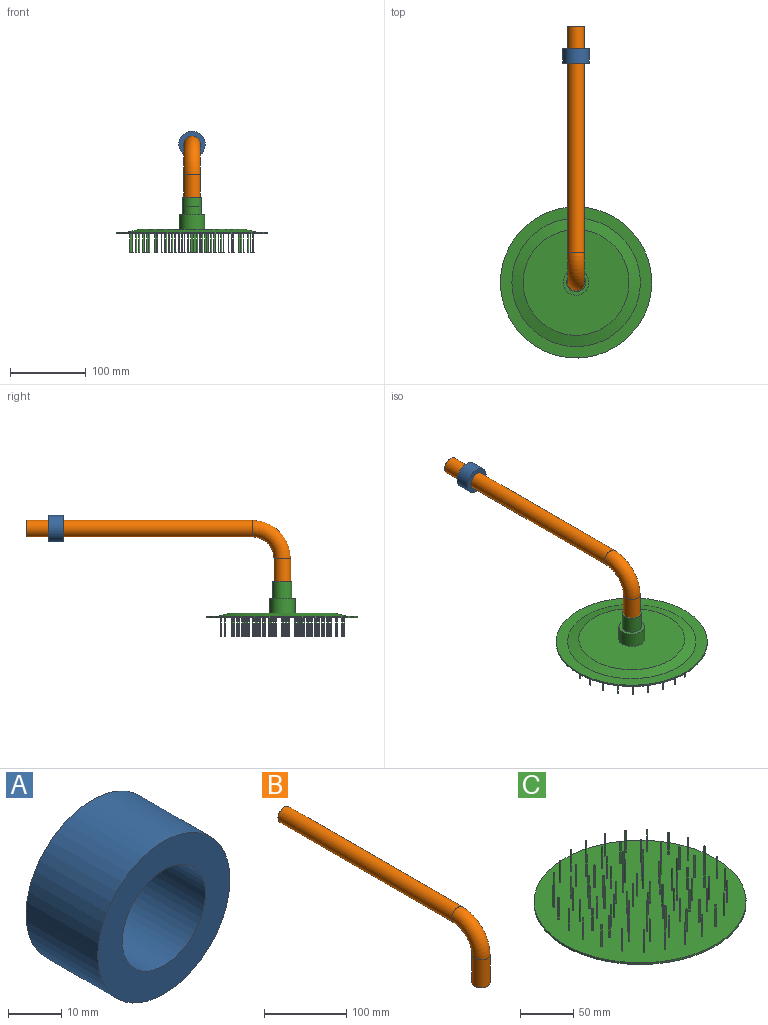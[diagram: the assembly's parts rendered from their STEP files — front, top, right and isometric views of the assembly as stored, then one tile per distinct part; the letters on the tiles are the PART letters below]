
ASSEMBLY  parts=3 mates=2
PART A: 4 faces, bbox 35x19x35 mm
  f0: cylinder r=11mm len=22mm, axis (0,1,0), area 1313.2mm2, adj f2,f3
  f1: cylinder r=17.5mm len=35mm, axis (0,1,0), area 2089.2mm2, adj f2,f3
  f2: plane 35x35mm, normal (0,-1,0), area 582mm2, adj f0,f1
  f3: plane 35x35mm, normal (0,1,0), area 582mm2, adj f0,f1
PART B: 5 faces, bbox 22x354.2x96.7 mm
  f0: plane 22x22mm, normal (0,1,0), area 380.1mm2, adj f2
  f1: plane 22x22mm, normal (0,0,-1), area 380.1mm2, adj f4
  f2: cylinder r=11mm len=299mm, axis (0,-1,0), area 20665.4mm2, adj f0,f3
  f3: torus R=40mm, axis (1,0,0), area 4342.6mm2, adj f2,f4
  f4: cylinder r=11mm len=41.5mm, axis (0,0,-1), area 2868.3mm2, adj f1,f3
PART C: 181 faces, bbox 200x200x73.5 mm
  f0: cylinder r=100mm len=200mm, axis (0,0,-1), area 1256.6mm2, adj f1,f2
  f1: plane 200x200mm, normal (0,0,1), area 31318.7mm2, adj f0,f9,f11,f13,f15,f17,f19,f21
  f2: plane 200x200mm, normal (0,0,-1), area 8756.2mm2, adj f0,f3
  f3: cone r=70mm half-angle=75deg, axis (0,0,1), area 7522.2mm2, adj f2,f4
  f4: plane 140x140mm, normal (0,0,-1), area 14485.9mm2, adj f3,f5
  f5: cylinder r=17mm len=34mm, axis (0,0,1), area 2136.3mm2, adj f4,f6
  f6: plane 34x34mm, normal (0,0,-1), area 417mm2, adj f5,f7
  f7: cylinder r=12.5mm len=25mm, axis (0,0,1), area 1767.1mm2, adj f6,f8
  f8: plane 25x25mm, normal (0,0,-1), area 490.9mm2, adj f7
  f9: cylinder r=0.6mm len=25mm, axis (0,0,-1), area 94.2mm2, adj f1,f10
  f10: plane 1.2x1.2mm, normal (0,0,1), area 1.1mm2, adj f9
  f11: cylinder r=0.6mm len=25mm, axis (0,0,-1), area 94.2mm2, adj f1,f12
  f12: plane 1.2x1.2mm, normal (0,0,1), area 1.1mm2, adj f11
  f13: cylinder r=0.6mm len=25mm, axis (0,0,-1), area 94.2mm2, adj f1,f14
  f14: plane 1.2x1.2mm, normal (0,0,1), area 1.1mm2, adj f13
  f15: cylinder r=0.6mm len=25mm, axis (0,0,-1), area 94.2mm2, adj f1,f16
  f16: plane 1.2x1.2mm, normal (0,0,1), area 1.1mm2, adj f15
  f17: cylinder r=0.6mm len=25mm, axis (0,0,-1), area 94.2mm2, adj f1,f18
  f18: plane 1.2x1.2mm, normal (0,0,1), area 1.1mm2, adj f17
  f19: cylinder r=0.6mm len=25mm, axis (0,0,-1), area 94.2mm2, adj f1,f20
  f20: plane 1.2x1.2mm, normal (0,0,1), area 1.1mm2, adj f19
  f21: cylinder r=0.6mm len=25mm, axis (0,0,-1), area 94.2mm2, adj f1,f22
  f22: plane 1.2x1.2mm, normal (0,0,1), area 1.1mm2, adj f21
  f23: cylinder r=0.6mm len=25mm, axis (0,0,-1), area 94.2mm2, adj f1,f24
  f24: plane 1.2x1.2mm, normal (0,0,1), area 1.1mm2, adj f23
  f25: cylinder r=0.6mm len=25mm, axis (0,0,-1), area 94.2mm2, adj f1,f26
  f26: plane 1.2x1.2mm, normal (0,0,1), area 1.1mm2, adj f25
  f27: cylinder r=0.6mm len=25mm, axis (0,0,-1), area 94.2mm2, adj f1,f28
  f28: plane 1.2x1.2mm, normal (0,0,1), area 1.1mm2, adj f27
  f29: cylinder r=0.6mm len=25mm, axis (0,0,-1), area 94.2mm2, adj f1,f30
  f30: plane 1.2x1.2mm, normal (0,0,1), area 1.1mm2, adj f29
  f31: cylinder r=0.6mm len=25mm, axis (0,0,-1), area 94.2mm2, adj f1,f32
  f32: plane 1.2x1.2mm, normal (0,0,1), area 1.1mm2, adj f31
  f33: cylinder r=0.6mm len=25mm, axis (0,0,-1), area 94.2mm2, adj f1,f34
  f34: plane 1.2x1.2mm, normal (0,0,1), area 1.1mm2, adj f33
  f35: cylinder r=0.6mm len=25mm, axis (0,0,-1), area 94.2mm2, adj f1,f36
  f36: plane 1.2x1.2mm, normal (0,0,1), area 1.1mm2, adj f35
  f37: cylinder r=0.6mm len=25mm, axis (0,0,-1), area 94.2mm2, adj f1,f38
  f38: plane 1.2x1.2mm, normal (0,0,1), area 1.1mm2, adj f37
  f39: cylinder r=0.6mm len=25mm, axis (0,0,-1), area 94.2mm2, adj f1,f40
  f40: plane 1.2x1.2mm, normal (0,0,1), area 1.1mm2, adj f39
  f41: cylinder r=0.6mm len=25mm, axis (0,0,-1), area 94.2mm2, adj f1,f42
  f42: plane 1.2x1.2mm, normal (0,0,1), area 1.1mm2, adj f41
  f43: cylinder r=0.6mm len=25mm, axis (0,0,-1), area 94.2mm2, adj f1,f44
  f44: plane 1.2x1.2mm, normal (0,0,1), area 1.1mm2, adj f43
  f45: cylinder r=0.6mm len=25mm, axis (0,0,-1), area 94.2mm2, adj f1,f46
  f46: plane 1.2x1.2mm, normal (0,0,1), area 1.1mm2, adj f45
  f47: cylinder r=0.6mm len=25mm, axis (0,0,-1), area 94.2mm2, adj f1,f48
  f48: plane 1.2x1.2mm, normal (0,0,1), area 1.1mm2, adj f47
  f49: cylinder r=0.6mm len=25mm, axis (0,0,-1), area 94.2mm2, adj f1,f50
  f50: plane 1.2x1.2mm, normal (0,0,1), area 1.1mm2, adj f49
  f51: cylinder r=0.6mm len=25mm, axis (0,0,-1), area 94.2mm2, adj f1,f52
  f52: plane 1.2x1.2mm, normal (0,0,1), area 1.1mm2, adj f51
  f53: cylinder r=0.6mm len=25mm, axis (0,0,-1), area 94.2mm2, adj f1,f54
  f54: plane 1.2x1.2mm, normal (0,0,1), area 1.1mm2, adj f53
  f55: cylinder r=0.6mm len=25mm, axis (0,0,-1), area 94.2mm2, adj f1,f56
  f56: plane 1.2x1.2mm, normal (0,0,1), area 1.1mm2, adj f55
  f57: cylinder r=0.6mm len=25mm, axis (0,0,-1), area 94.2mm2, adj f1,f58
  f58: plane 1.2x1.2mm, normal (0,0,1), area 1.1mm2, adj f57
  f59: cylinder r=0.6mm len=25mm, axis (0,0,-1), area 94.2mm2, adj f1,f60
  f60: plane 1.2x1.2mm, normal (0,0,1), area 1.1mm2, adj f59
  f61: cylinder r=0.6mm len=25mm, axis (0,0,-1), area 94.2mm2, adj f1,f62
  f62: plane 1.2x1.2mm, normal (0,0,1), area 1.1mm2, adj f61
  f63: cylinder r=0.6mm len=25mm, axis (0,0,-1), area 94.2mm2, adj f1,f64
  f64: plane 1.2x1.2mm, normal (0,0,1), area 1.1mm2, adj f63
  f65: cylinder r=0.6mm len=25mm, axis (0,0,-1), area 94.2mm2, adj f1,f66
  f66: plane 1.2x1.2mm, normal (0,0,1), area 1.1mm2, adj f65
  f67: cylinder r=0.6mm len=25mm, axis (0,0,-1), area 94.2mm2, adj f1,f68
  f68: plane 1.2x1.2mm, normal (0,0,1), area 1.1mm2, adj f67
  f69: cylinder r=0.6mm len=25mm, axis (0,0,-1), area 94.2mm2, adj f1,f70
  f70: plane 1.2x1.2mm, normal (0,0,1), area 1.1mm2, adj f69
  f71: cylinder r=0.6mm len=25mm, axis (0,0,-1), area 94.2mm2, adj f1,f72
  f72: plane 1.2x1.2mm, normal (0,0,1), area 1.1mm2, adj f71
  f73: cylinder r=0.6mm len=25mm, axis (0,0,-1), area 94.2mm2, adj f1,f74
  f74: plane 1.2x1.2mm, normal (0,0,1), area 1.1mm2, adj f73
  f75: cylinder r=0.6mm len=25mm, axis (0,0,-1), area 94.2mm2, adj f1,f76
  f76: plane 1.2x1.2mm, normal (0,0,1), area 1.1mm2, adj f75
  f77: cylinder r=0.6mm len=25mm, axis (0,0,-1), area 94.2mm2, adj f1,f78
  f78: plane 1.2x1.2mm, normal (0,0,1), area 1.1mm2, adj f77
  f79: cylinder r=0.6mm len=25mm, axis (0,0,-1), area 94.2mm2, adj f1,f80
  f80: plane 1.2x1.2mm, normal (0,0,1), area 1.1mm2, adj f79
  f81: cylinder r=0.6mm len=25mm, axis (0,0,-1), area 94.2mm2, adj f1,f82
  f82: plane 1.2x1.2mm, normal (0,0,1), area 1.1mm2, adj f81
  f83: cylinder r=0.6mm len=25mm, axis (0,0,-1), area 94.2mm2, adj f1,f84
  f84: plane 1.2x1.2mm, normal (0,0,1), area 1.1mm2, adj f83
  f85: cylinder r=0.6mm len=25mm, axis (0,0,-1), area 94.2mm2, adj f1,f86
  f86: plane 1.2x1.2mm, normal (0,0,1), area 1.1mm2, adj f85
  f87: cylinder r=0.6mm len=25mm, axis (0,0,-1), area 94.2mm2, adj f1,f88
  f88: plane 1.2x1.2mm, normal (0,0,1), area 1.1mm2, adj f87
  f89: cylinder r=0.6mm len=25mm, axis (0,0,-1), area 94.2mm2, adj f1,f90
  f90: plane 1.2x1.2mm, normal (0,0,1), area 1.1mm2, adj f89
  f91: cylinder r=0.6mm len=25mm, axis (0,0,-1), area 94.2mm2, adj f1,f92
  f92: plane 1.2x1.2mm, normal (0,0,1), area 1.1mm2, adj f91
  f93: cylinder r=0.6mm len=25mm, axis (0,0,-1), area 94.2mm2, adj f1,f94
  f94: plane 1.2x1.2mm, normal (0,0,1), area 1.1mm2, adj f93
  f95: cylinder r=0.6mm len=25mm, axis (0,0,-1), area 94.2mm2, adj f1,f96
  f96: plane 1.2x1.2mm, normal (0,0,1), area 1.1mm2, adj f95
  f97: cylinder r=0.6mm len=25mm, axis (0,0,-1), area 94.2mm2, adj f1,f98
  f98: plane 1.2x1.2mm, normal (0,0,1), area 1.1mm2, adj f97
  f99: cylinder r=0.6mm len=25mm, axis (0,0,-1), area 94.2mm2, adj f1,f100
  f100: plane 1.2x1.2mm, normal (0,0,1), area 1.1mm2, adj f99
  f101: cylinder r=0.6mm len=25mm, axis (0,0,-1), area 94.2mm2, adj f1,f102
  f102: plane 1.2x1.2mm, normal (0,0,1), area 1.1mm2, adj f101
  f103: cylinder r=0.6mm len=25mm, axis (0,0,-1), area 94.2mm2, adj f1,f104
  f104: plane 1.2x1.2mm, normal (0,0,1), area 1.1mm2, adj f103
  f105: cylinder r=0.6mm len=25mm, axis (0,0,-1), area 94.2mm2, adj f1,f106
  f106: plane 1.2x1.2mm, normal (0,0,1), area 1.1mm2, adj f105
  f107: cylinder r=0.6mm len=25mm, axis (0,0,-1), area 94.2mm2, adj f1,f108
  f108: plane 1.2x1.2mm, normal (0,0,1), area 1.1mm2, adj f107
  f109: cylinder r=0.6mm len=25mm, axis (0,0,-1), area 94.2mm2, adj f1,f110
  f110: plane 1.2x1.2mm, normal (0,0,1), area 1.1mm2, adj f109
  f111: cylinder r=0.6mm len=25mm, axis (0,0,-1), area 94.2mm2, adj f1,f112
  f112: plane 1.2x1.2mm, normal (0,0,1), area 1.1mm2, adj f111
  f113: cylinder r=0.6mm len=25mm, axis (0,0,-1), area 94.2mm2, adj f1,f114
  f114: plane 1.2x1.2mm, normal (0,0,1), area 1.1mm2, adj f113
  f115: cylinder r=0.6mm len=25mm, axis (0,0,-1), area 94.2mm2, adj f1,f116
  f116: plane 1.2x1.2mm, normal (0,0,1), area 1.1mm2, adj f115
  f117: cylinder r=0.6mm len=25mm, axis (0,0,-1), area 94.2mm2, adj f1,f118
  f118: plane 1.2x1.2mm, normal (0,0,1), area 1.1mm2, adj f117
  f119: cylinder r=0.6mm len=25mm, axis (0,0,-1), area 94.2mm2, adj f1,f120
  f120: plane 1.2x1.2mm, normal (0,0,1), area 1.1mm2, adj f119
  f121: cylinder r=0.6mm len=25mm, axis (0,0,-1), area 94.2mm2, adj f1,f122
  f122: plane 1.2x1.2mm, normal (0,0,1), area 1.1mm2, adj f121
  f123: cylinder r=0.6mm len=25mm, axis (0,0,-1), area 94.2mm2, adj f1,f124
  f124: plane 1.2x1.2mm, normal (0,0,1), area 1.1mm2, adj f123
  f125: cylinder r=0.6mm len=25mm, axis (0,0,-1), area 94.2mm2, adj f1,f126
  f126: plane 1.2x1.2mm, normal (0,0,1), area 1.1mm2, adj f125
  f127: cylinder r=0.6mm len=25mm, axis (0,0,-1), area 94.2mm2, adj f1,f128
  f128: plane 1.2x1.2mm, normal (0,0,1), area 1.1mm2, adj f127
  f129: cylinder r=0.6mm len=25mm, axis (0,0,-1), area 94.2mm2, adj f1,f130
  f130: plane 1.2x1.2mm, normal (0,0,1), area 1.1mm2, adj f129
  f131: cylinder r=0.6mm len=25mm, axis (0,0,-1), area 94.2mm2, adj f1,f132
  f132: plane 1.2x1.2mm, normal (0,0,1), area 1.1mm2, adj f131
  f133: cylinder r=0.6mm len=25mm, axis (0,0,-1), area 94.2mm2, adj f1,f134
  f134: plane 1.2x1.2mm, normal (0,0,1), area 1.1mm2, adj f133
  f135: cylinder r=0.6mm len=25mm, axis (0,0,-1), area 94.2mm2, adj f1,f136
  f136: plane 1.2x1.2mm, normal (0,0,1), area 1.1mm2, adj f135
  f137: cylinder r=0.6mm len=25mm, axis (0,0,-1), area 94.2mm2, adj f1,f138
  f138: plane 1.2x1.2mm, normal (0,0,1), area 1.1mm2, adj f137
  f139: cylinder r=0.6mm len=25mm, axis (0,0,-1), area 94.2mm2, adj f1,f140
  f140: plane 1.2x1.2mm, normal (0,0,1), area 1.1mm2, adj f139
  f141: cylinder r=0.6mm len=25mm, axis (0,0,-1), area 94.2mm2, adj f1,f142
  f142: plane 1.2x1.2mm, normal (0,0,1), area 1.1mm2, adj f141
  f143: cylinder r=0.6mm len=25mm, axis (0,0,-1), area 94.2mm2, adj f1,f144
  f144: plane 1.2x1.2mm, normal (0,0,1), area 1.1mm2, adj f143
  f145: cylinder r=0.6mm len=25mm, axis (0,0,-1), area 94.2mm2, adj f1,f146
  f146: plane 1.2x1.2mm, normal (0,0,1), area 1.1mm2, adj f145
  f147: cylinder r=0.6mm len=25mm, axis (0,0,-1), area 94.2mm2, adj f1,f148
  f148: plane 1.2x1.2mm, normal (0,0,1), area 1.1mm2, adj f147
  f149: cylinder r=0.6mm len=25mm, axis (0,0,-1), area 94.2mm2, adj f1,f150
  f150: plane 1.2x1.2mm, normal (0,0,1), area 1.1mm2, adj f149
  f151: cylinder r=0.6mm len=25mm, axis (0,0,-1), area 94.2mm2, adj f1,f152
  f152: plane 1.2x1.2mm, normal (0,0,1), area 1.1mm2, adj f151
  f153: cylinder r=0.6mm len=25mm, axis (0,0,-1), area 94.2mm2, adj f1,f154
  f154: plane 1.2x1.2mm, normal (0,0,1), area 1.1mm2, adj f153
  f155: cylinder r=0.6mm len=25mm, axis (0,0,-1), area 94.2mm2, adj f1,f156
  f156: plane 1.2x1.2mm, normal (0,0,1), area 1.1mm2, adj f155
  f157: cylinder r=0.6mm len=25mm, axis (0,0,-1), area 94.2mm2, adj f1,f158
  f158: plane 1.2x1.2mm, normal (0,0,1), area 1.1mm2, adj f157
  f159: cylinder r=0.6mm len=25mm, axis (0,0,-1), area 94.2mm2, adj f1,f160
  f160: plane 1.2x1.2mm, normal (0,0,1), area 1.1mm2, adj f159
  f161: cylinder r=0.6mm len=25mm, axis (0,0,-1), area 94.2mm2, adj f1,f162
  f162: plane 1.2x1.2mm, normal (0,0,1), area 1.1mm2, adj f161
  f163: cylinder r=0.6mm len=25mm, axis (0,0,-1), area 94.2mm2, adj f1,f164
  f164: plane 1.2x1.2mm, normal (0,0,1), area 1.1mm2, adj f163
  f165: cylinder r=0.6mm len=25mm, axis (0,0,-1), area 94.2mm2, adj f1,f166
  f166: plane 1.2x1.2mm, normal (0,0,1), area 1.1mm2, adj f165
  f167: cylinder r=0.6mm len=25mm, axis (0,0,-1), area 94.2mm2, adj f1,f168
  f168: plane 1.2x1.2mm, normal (0,0,1), area 1.1mm2, adj f167
  f169: cylinder r=0.6mm len=25mm, axis (0,0,-1), area 94.2mm2, adj f1,f170
  f170: plane 1.2x1.2mm, normal (0,0,1), area 1.1mm2, adj f169
  f171: cylinder r=0.6mm len=25mm, axis (0,0,-1), area 94.2mm2, adj f1,f172
  f172: plane 1.2x1.2mm, normal (0,0,1), area 1.1mm2, adj f171
  f173: cylinder r=0.6mm len=25mm, axis (0,0,-1), area 94.2mm2, adj f1,f174
  f174: plane 1.2x1.2mm, normal (0,0,1), area 1.1mm2, adj f173
  f175: cylinder r=0.6mm len=25mm, axis (0,0,-1), area 94.2mm2, adj f1,f176
  f176: plane 1.2x1.2mm, normal (0,0,1), area 1.1mm2, adj f175
  f177: cylinder r=0.6mm len=25mm, axis (0,0,-1), area 94.2mm2, adj f1,f178
  f178: plane 1.2x1.2mm, normal (0,0,1), area 1.1mm2, adj f177
  f179: cylinder r=0.6mm len=25mm, axis (0,0,-1), area 94.2mm2, adj f1,f180
  f180: plane 1.2x1.2mm, normal (0,0,1), area 1.1mm2, adj f179
PLACE A t=(-160.16,198.58,-58.19)mm
PLACE B t=(-160.16,122.64,-58.19)mm
PLACE C rot(axis=(0,1,0),180deg) t=(-160.16,-510.42,-174.19)mm
MATE fastened B.f2 <-> A.f1  axis (0,1,0) through (-160.16,-171.42,-58.19)mm
MATE fastened B.f4 <-> C.f7  axis (0,0,-1) through (-160.16,-510.42,-139.69)mm
